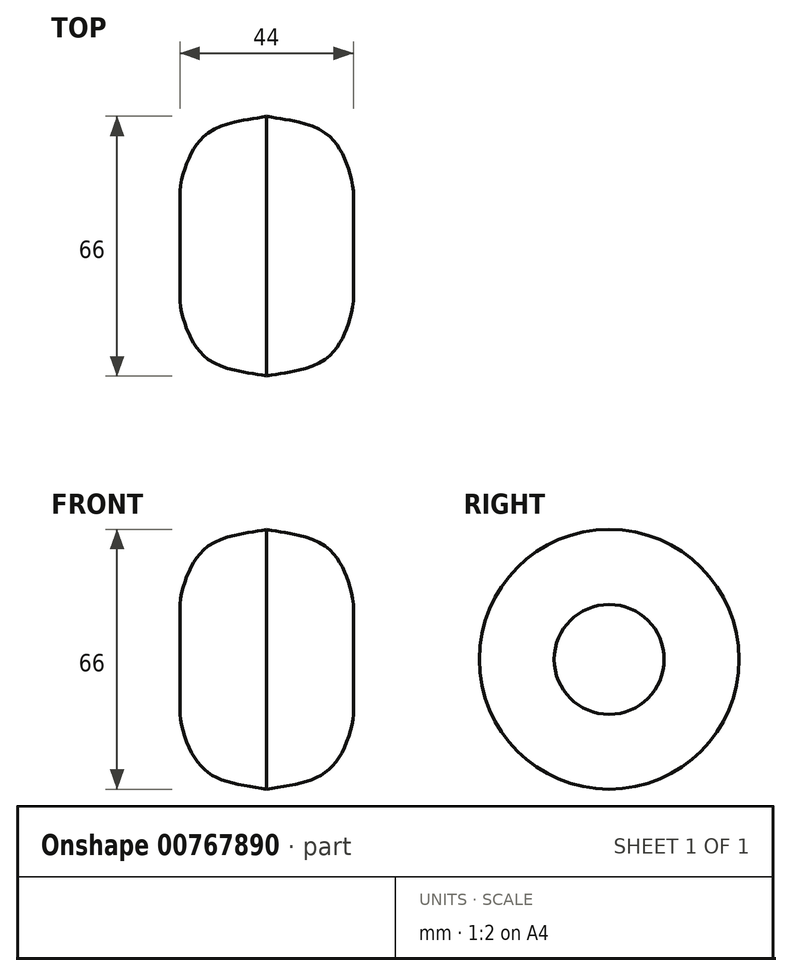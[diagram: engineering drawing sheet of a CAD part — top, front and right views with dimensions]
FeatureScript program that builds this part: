
annotation { "Feature Type Name" : "Feature", "Feature Type Description" : "" }
export const myFeature = defineFeature(function(context is Context, id is Id, definition is map)
    precondition{}
    {
        {
            var Q0;
            Q0=qCreatedBy(makeId("Front.planeOp"),FACE);
            var sketch = newSketch(context, id + "F0", { "sketchPlane" : qUnion([Q0])});
            skLineSegment(sketch, "E0", {"start": v(0, 0) * mm, "end": v(0, 33) * mm});
            skLineSegment(sketch, "E1", {"start": v(0, 0) * mm, "end": v(-22, 0) * mm});
            skLineSegment(sketch, "E2", {"start": v(-22, 0) * mm, "end": v(-22, 13.96) * mm});
            skFitSpline(sketch, "E3", {"points": [v(0, 33) * mm, v(-11.51, 30.54) * mm, v(-18.38, 24.92) * mm, v(-22, 13.96) * mm], "startDerivative": vector(-30.6, -5.79) * mm, "endDerivative": vector(-1.59, -28) * mm});
            skSolve(sketch);
        }
        {
            var Q0;
            Q0=makeQuery(id+"F0.imprint","IMPRINT",FACE,{"disambiguationData":[TD([[makeQuery(id+"F0.imprint","IMPRINT",EDGE,{"derivedFrom":sQuery(id+"F0.wireOp",EDGE,"E0")}),1.0]])]});
            var Q1;
            Q1=sQuery(id+"F0.wireOp",EDGE,"E1");
            revolve(context, id + "F1", {"surfaceOperationType" : NewSurfaceOperationType.NEW, "entities" : qUnion([Q0]), "axis" : qUnion([Q1]), "revolveType" : RevolveType.FULL});
        }
        {
            var Q0;
            Q0=makeQuery(id+"F1.opRevolve","SWEPT_BODY",BODY,{"disambiguationData":[OSD([sQuery(id+"F0.wireOp",EDGE,"E0"),sQuery(id+"F0.wireOp",EDGE,"E1"),sQuery(id+"F0.wireOp",EDGE,"E2"),sQuery(id+"F0.wireOp",EDGE,"E3")])]});
            var Q1;
            Q1=qCreatedBy(makeId("Right.planeOp"),FACE);
            mirror(context, id + "F2", {"entities" : qUnion([Q0]), "mirrorPlane" : qUnion([Q1])});
        }
    });
